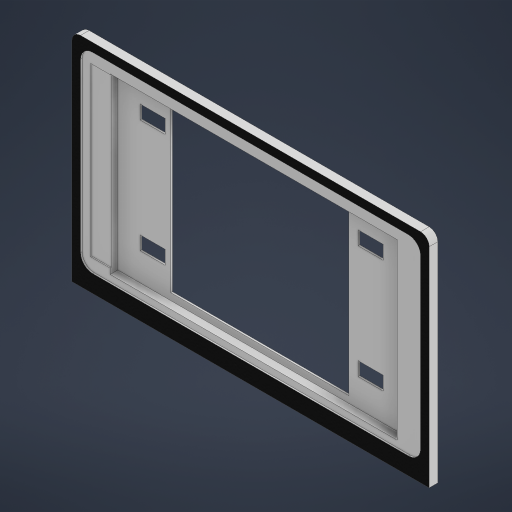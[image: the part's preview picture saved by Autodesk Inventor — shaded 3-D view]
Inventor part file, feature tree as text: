
AUTODESK INVENTOR PART (.ipt)
format: ipt  version: 2024.2 (Build 282272000, 272)  size: 624,128 bytes
history: native  units: mm
features: projected_geometry x7, extrude x6, sketch x6, other x4, reference x1
ambient origin geometry x8: Origin, YZ Plane, XZ Plane, XY Plane, X Axis, Y Axis, Z Axis, Center Point
bodies: Body1 (feature_tree)
feature tree (24):
  other  "솔리드1"
  extrude  "돌출1"  Depth=5.0mm TaperAngle=0.0deg
  extrude  "돌출2"  Depth=197.0mm
  sketch  "스케치3"
  extrude  "돌출4"  Depth=111.0mm
  extrude  "돌출5"  Depth=207.0mm
  extrude  "돌출6"  Depth=126.0mm
  extrude  "돌출8"  Depth=103.5mm
  sketch  "스케치1"
  reference  "참조1"
  sketch  "스케치2"
  projected_geometry  "투영된 루프1"
  projected_geometry  "투영된 루프2"
  sketch  "스케치4"
  projected_geometry  "투영된 루프3"
  sketch  "스케치6"
  projected_geometry  "투영된 루프4"
  sketch  "스케치8"
  projected_geometry  "투영된 루프5"
  projected_geometry  "투영된 루프6"
  projected_geometry  "투영된 루프7"
  other  "<userpath>\Downloads\AAST\PART\AAST Remote Controler\AASTRC case.iam"
  other  "AASTRC case.iam"
  other  "AASTRC Bottom case:1"
